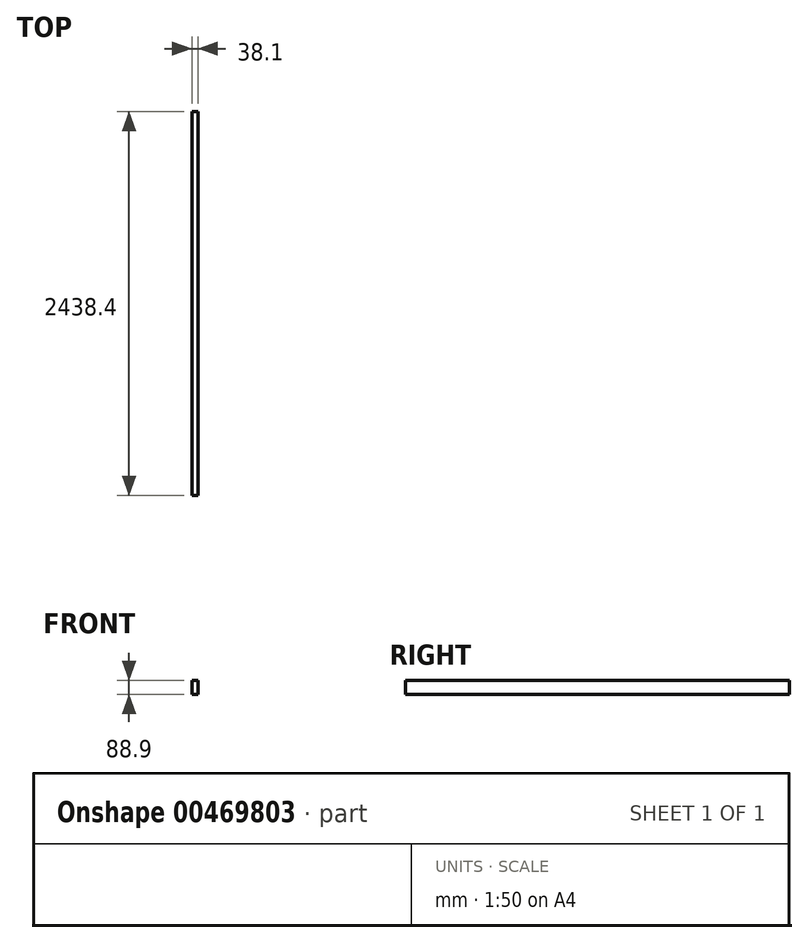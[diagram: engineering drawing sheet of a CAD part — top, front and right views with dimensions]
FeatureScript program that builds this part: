
annotation { "Feature Type Name" : "Feature", "Feature Type Description" : "" }
export const myFeature = defineFeature(function(context is Context, id is Id, definition is map)
    precondition{}
    {
        {
            var Q0;
            Q0=qCreatedBy(makeId("Front.planeOp"),FACE);
            var sketch = newSketch(context, id + "F0", { "sketchPlane" : qUnion([Q0])});
            skLineSegment(sketch, "E0.bottom", {"start": v(19.05, 44.45) * mm, "end": v(-19.05, 44.45) * mm});
            skLineSegment(sketch, "E0.top", {"start": v(19.05, -44.45) * mm, "end": v(-19.05, -44.45) * mm});
            skLineSegment(sketch, "E0.left", {"start": v(19.05, 44.45) * mm, "end": v(19.05, -44.45) * mm});
            skLineSegment(sketch, "E0.right", {"start": v(-19.05, 44.45) * mm, "end": v(-19.05, -44.45) * mm});
            skPoint(sketch, "E0.middle", {"position": v(0, 0) * mm});
            skSolve(sketch);
        }
        {
            var Q0;
            Q0=qSketchRegion(id+"F0",true);
            extrude(context, id + "F1", {"entities" : qUnion([Q0]), "oppositeDirection" : true, "depth" : 2438.4 * mm});
        }
    });
